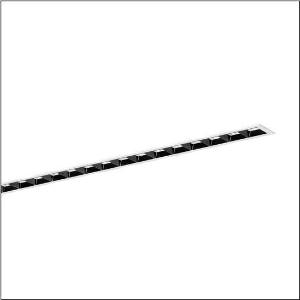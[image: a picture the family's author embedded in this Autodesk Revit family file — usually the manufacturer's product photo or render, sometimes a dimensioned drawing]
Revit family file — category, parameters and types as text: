
# Revit family: silica_r__21_51mx12tbt5w_1d14
name_source: partatom
category: Lighting Fixtures
units: mm (PartAtom-declared; Revit-internal decimal feet)

## family parameters
Cut with Voids When Loaded = No
Host = Face
Light Source = No
Part Type = Normal
Room Calculation Point = No
Round Connector Dimension = Use Diameter
Shared = No

## types (1)
- --- (1 x LED, 4650 lm, 40.2 W, 6500K)
    Apparent Load = 40 VA
    CIE Flux Codes = 84 100 100 100 100
    Color Rendering = 80
    Color Temperature = 6500K
    Default Elevation = 1800 mm
    Description = Silica® 21, office luminaire, primary light control with darklight reflector, of PMMA, black, CAT 2 (L<= 3000cd/m²), light emission: direct distribution, primary light characteristic: symmetric, installation type: recessed, LED, rated luminous flux: 4.650lm, luminous efficacy: 110lm/W, light colour: 8tw, colour temperature: 2700..6500K, with terminal, 3+2-pole, max. 2.5mm², mains connection: 220..240V, AC, 50/60Hz, rated input power: 42.2W, luminaire housing, of aluminium, traffic white (RAL 9016), length: 1.528mm, width: 79mm, height: 53mm, protection rating (complete): IP20, insulation class (complete): insulation class I (protective earthing), certification: CE, permissible operating ambient temperature: 0..+35°C, standard: EN 50419, packaging unit: 1 piece
    Height = 0 mm  [stored 0 ft]
    Lamp = 1 x LED
    Lamp Light Flux = 4650 lm
    Lamp Power = 40.2 W
    Lamp count = 1
    Length = 1527 mm
    Luminous efficacy = 116 lm/W
    Manufacturer = Siteco
    ModVariant = No
    Model = 51MX12TBT5W
    Mounting Place = Ceiling
    Mounting Type = Recessed
    Number of Poles = 1
    OnlyDefault = Yes
    Power Factor = 1
    Product Name = Silica® 21
    Product group = office luminaire | ceiling recessed
    ProductGroupID = 401
    Protection Class = Protection class I
    Protection Degree = IP 20
    RLX_Detail_Level = 1
    RLX_Emergency_Light_Flux = 0 lm
    RLX_Emergency_Type = 0
    RLX_Emergency_Type_DB = No
    RlxData = <blob elided: 38985 chars, md5=f9f07aa9>
    Socket = socket
    Standby Power = 0 W
    System Light Flux = 4650 lm
    System Power = 40 W
    Type Comments = individual setting
    Type Image = l_1297791.jpg
    URL = http://relux.com
    VarID = @adj_071497
    Voltage = 0 V
    Weight = 0.00 kg
    Width = 79 mm

note: [stored X ft] marks values corroborated as IEEE doubles in the binary element streams (Revit-internal decimal feet)

## geometry (parser evidence)
native form markers: Blend x4, Sweep x9
no freeform markers — native parametric forms only
